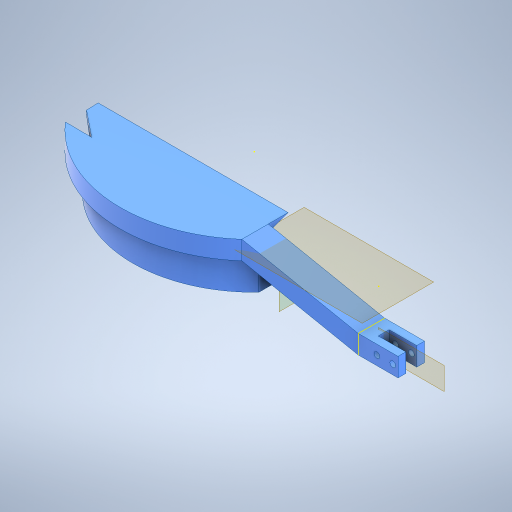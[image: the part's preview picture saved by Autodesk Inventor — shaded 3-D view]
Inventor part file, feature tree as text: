
AUTODESK INVENTOR PART (.ipt)
format: ipt  version: 2024.3 (Build 283343000, 343)  size: 393,216 bytes
history: native  units: mm
features: sketch x12, projected_geometry x8, extrude x7, other x4, plane x3, reference x3, mirror x1, loft x1, sweep x1, chamfer x1
ambient origin geometry x8: Origin, YZ Plane, XZ Plane, XY Plane, X Axis, Y Axis, Z Axis, Center Point
bodies: Solid1 (feature_tree)
feature tree (41):
  sketch  "Sketch1"  dims[d0=5.0mm d1=0.0mm d2=0.2mm d3=0.0mm]
  plane  "Work Plane1"
  extrude  "Extrusion1"  Depth=5.0mm TaperAngle=0.0deg
  mirror  "Mirror1"
  extrude  "Extrusion2"  Depth=8.0mm
  extrude  "Extrusion3"  Depth=12.0mm
  plane  "Work Plane2"
  sketch  "Sketch4"  dims[d11=0.0mm d12=90.0deg d13=0.0mm d14=90.0deg]
  sketch  "Sketch5"  dims[d16=45.748737mm d17=16.248737mm]
  loft  "Loft1"
  sketch  "Sketch6"  dims[d18=0.0mm d19=0.0mm d20=8.0mm d21=0.0mm d22=22.0mm d23=8.0mm d24=45.0deg]
  plane  "Work Plane3"
  sweep  "Sweep1"
  sketch  "Sketch8"  dims[d28=3.0mm d29=0.0mm d30=0.2mm]
  extrude  "Extrusion4"  Depth=8.0mm TaperAngle=0.0deg
  chamfer  "Chamfer1"  Distance=8.0mm Angle=45.0deg
  extrude  "Extrusion5"  Depth=20.0mm TaperAngle=0.0deg
  extrude  "Extrusion6"  Depth=3.0mm
  extrude  "Extrusion7"  Depth=50.0mm TaperAngle=0.0deg
  reference  "Reference1"
  sketch  "Sketch2"  dims[d4=8.0mm d5=0.0mm d6=50.0mm]
  projected_geometry  "Projected Loop1"
  reference  "Reference2"
  projected_geometry  "Projected Loop2"
  sketch  "Sketch3"  dims[d9=17.0mm d10=12.0mm]
  projected_geometry  "Projected Loop3"
  reference  "Reference3"
  projected_geometry  "Projected Loop4"
  projected_geometry  "Projected Loop5"
  projected_geometry  "Projected Loop6"
  other  "Edges1"
  projected_geometry  "Projected Loop7"
  sketch  "Sketch7"  dims[d25=4.0mm d26=20.0mm d27=0.0mm]
  sketch  "Sketch9"  dims[d31=0.2mm d32=50.0mm d33=0.0mm]
  sketch  "Sketch10"
  sketch  "Sketch11"
  projected_geometry  "Projected Loop8"
  sketch  "Sketch12"
  other  "Assembly1"
  other  "dedos:1"
  other  "housing:1"
